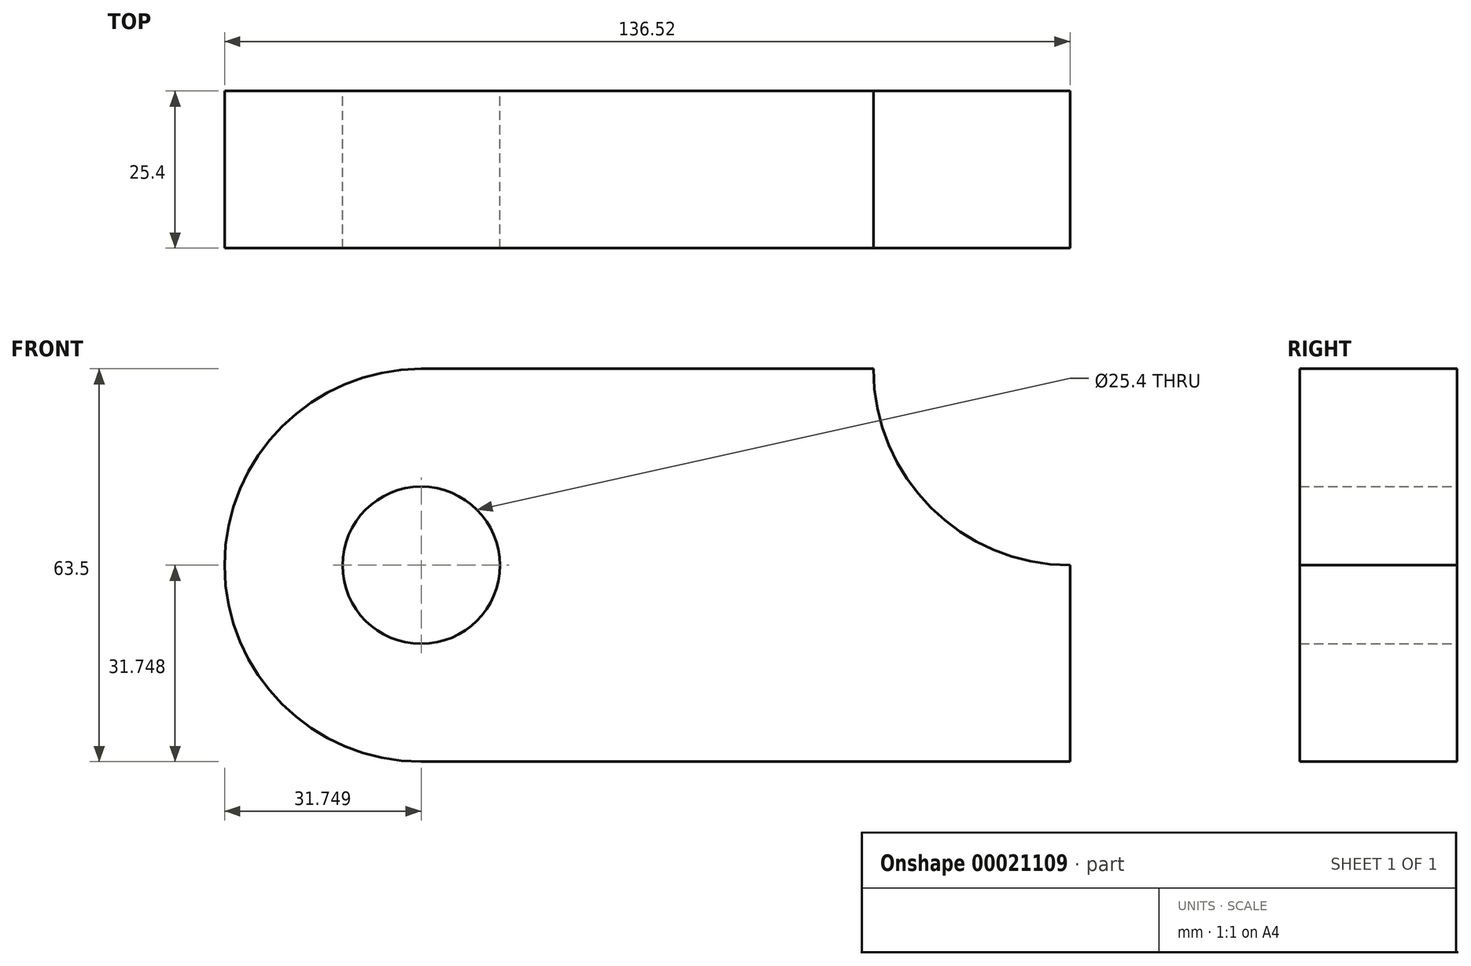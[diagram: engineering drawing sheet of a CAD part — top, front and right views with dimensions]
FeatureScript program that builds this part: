
annotation { "Feature Type Name" : "Feature", "Feature Type Description" : "" }
export const myFeature = defineFeature(function(context is Context, id is Id, definition is map)
    precondition{}
    {
        {
            var Q0;
            Q0=qCreatedBy(makeId("Front.planeOp"),FACE);
            var sketch = newSketch(context, id + "F0", { "sketchPlane" : qUnion([Q0])});
            skLineSegment(sketch, "E0.bottom", {"start": v(-69.91, 23.59) * mm, "end": v(34.86, 23.59) * mm});
            skLineSegment(sketch, "E0.top", {"start": v(-69.91, -39.91) * mm, "end": v(34.86, -39.91) * mm});
            skLineSegment(sketch, "E0.left", {"start": v(-69.91, 23.59) * mm, "end": v(-69.91, -39.91) * mm});
            skLineSegment(sketch, "E0.right", {"start": v(34.86, 23.59) * mm, "end": v(34.86, -39.91) * mm});
            skCircle(sketch, "E1", {"center": v(-69.91, -8.16) * mm, "radius": 31.75 * mm});
            skCircle(sketch, "E2", {"center": v(-69.91, -8.16) * mm, "radius": 12.7 * mm});
            skCircle(sketch, "E3", {"center": v(34.86, 23.59) * mm, "radius": 31.75 * mm});
            skSolve(sketch);
        }
        {
            var Q0;
            {var subQ0=sQuery(id+"F0.wireOp",EDGE,"E2");var subQ1=sQuery(id+"F0.wireOp",EDGE,"E0.left");var subQ3=makeQuery(id+"F0.imprint","INTERSECT",VERTEX,{"disambiguationData":[OD(0.0)],"derivedFrom":[subQ1,subQ0]});Q0=makeQuery(id+"F0.imprint","IMPRINT",FACE,{"disambiguationData":[TD([[makeQuery(id+"F0.imprint","IMPRINT",EDGE,{"disambiguationData":[TD([[subQ3,1.0]])],"derivedFrom":subQ0}),-1.0]])]});}
            var Q1;
            {var subQ0=sQuery(id+"F0.wireOp",EDGE,"E2");var subQ1=sQuery(id+"F0.wireOp",EDGE,"E0.left");var subQ3=makeQuery(id+"F0.imprint","INTERSECT",VERTEX,{"disambiguationData":[OD(0.0)],"derivedFrom":[subQ1,subQ0]});Q1=makeQuery(id+"F0.imprint","IMPRINT",FACE,{"disambiguationData":[TD([[makeQuery(id+"F0.imprint","IMPRINT",EDGE,{"disambiguationData":[TD([[subQ3,-1.0]])],"derivedFrom":subQ0}),-1.0]])]});}
            var Q2;
            {var subQ6=sQuery(id+"F0.wireOp",EDGE,"E0.top");Q2=makeQuery(id+"F0.imprint","IMPRINT",FACE,{"disambiguationData":[TD([[makeQuery(id+"F0.imprint","IMPRINT",EDGE,{"derivedFrom":subQ6}),1.0]])]});}
            extrude(context, id + "F1", {"entities" : qUnion([Q0, Q1, Q2]), "depth" : 25.4 * mm});
        }
    });
